# Revit family: 206_566bada093ca4c2b9aefe1cd1d3ebc
name_source: partatom
category: Duct Accessories
revit_build: Autodesk Revit 2018 (Build: 20170223_1515(x64)
units: mm (PartAtom-declared; Revit-internal decimal feet)

## family parameters
Always vertical = Yes
Cut with Voids When Loaded = No
Part Type = Breaks Into
Round Connector Dimension = Use Diameter
Shared = No
Work Plane-Based = No

## types (5) — shared parameters
CAT0 = Yes
Description = Flat roof socket DSF
H2D = 305 mm  [stored 1.00066 ft]
L2D = 297 mm  [stored 0.974409 ft]
Manufacturer = Flexit
SH = 30 mm  [stored 0.0984252 ft]
URL = www.flexit.no
W2D = 305 mm  [stored 1.00066 ft]
X1 = 2 mm  [stored 0.00656168 ft]
magiPartTypeId = 206
magiProductFamilyId = 566bada093ca4c2b9aefe1cd1d3ebc

## per-type parameters (varying)
| type | A | A__ve | B | BT2 | H | H1 | HT2 | L | L1 | LT2 | magiProductId |
| 114677 | 457 mm  [stored 1.49934 ft] | -457 mm  [stored -1.49934 ft] | 245 mm | 123 mm | 245 mm | 305 mm  [stored 1.00066 ft] | 123 mm | 297 mm  [stored 0.974409 ft] | 295 mm | 149 mm | 1faf4fd2dfb24100a7ba8ce3c4cab6 |
| 114678 | 557 mm | -557 mm | 330 mm | 165 mm  [stored 0.541339 ft] | 330 mm | 390 mm | 165 mm  [stored 0.541339 ft] | 299 mm  [stored 0.980971 ft] | 297 mm  [stored 0.974409 ft] | 150 mm | 970b51eb6d8a4a4fae6d7d237baf50 |
| 114679 | 757 mm | -757 mm | 450 mm | 225 mm | 450 mm | 510 mm | 225 mm | 299 mm  [stored 0.980971 ft] | 297 mm  [stored 0.974409 ft] | 150 mm | ed4e56ca92cb41e3ad36591fe9c343 |
| 114680 | 815 mm | -815 mm | 535 mm | 268 mm | 535 mm | 595 mm | 268 mm | 299 mm  [stored 0.980971 ft] | 297 mm  [stored 0.974409 ft] | 150 mm | 785f27c8b5c44eeab7c6487ef76919 |
| 114681 | 1097 mm  [stored 3.59908 ft] | -1097 mm  [stored -3.59908 ft] | 750 mm | 375 mm  [stored 1.23031 ft] | 750 mm | 810 mm  [stored 2.65748 ft] | 375 mm  [stored 1.23031 ft] | 301 mm  [stored 0.987533 ft] | 299 mm  [stored 0.980971 ft] | 151 mm | 595ef0570db64860a92aa5288a7b03 |

note: column(s) folded — value = type name in every type: MC Product Code

note: [stored X ft] marks values corroborated as IEEE doubles in the binary element streams (Revit-internal decimal feet)

## geometry (parser evidence)
native form markers: Sweep x2
no freeform markers — native parametric forms only
